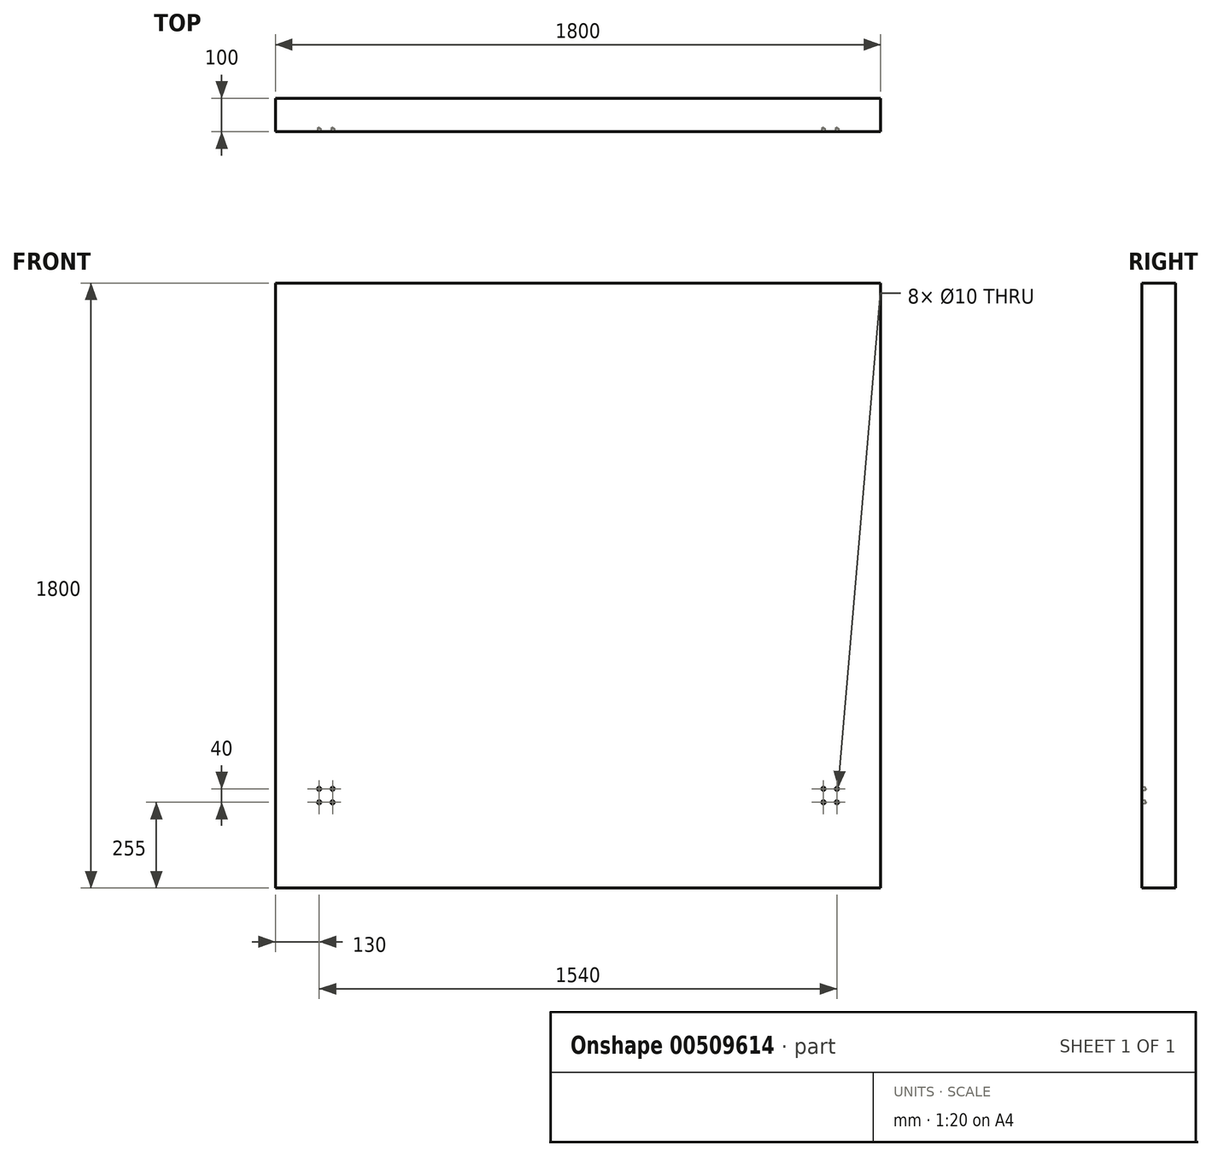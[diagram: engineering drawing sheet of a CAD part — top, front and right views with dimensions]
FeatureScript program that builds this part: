
annotation { "Feature Type Name" : "Feature", "Feature Type Description" : "" }
export const myFeature = defineFeature(function(context is Context, id is Id, definition is map)
    precondition{}
    {
        {
            var Q0;
            Q0=qCreatedBy(makeId("Front.planeOp"),FACE);
            var sketch = newSketch(context, id + "F0", { "sketchPlane" : qUnion([Q0])});
            skLineSegment(sketch, "E0.bottom", {"start": v(-900, 900) * mm, "end": v(900, 900) * mm});
            skLineSegment(sketch, "E0.top", {"start": v(-900, -900) * mm, "end": v(900, -900) * mm});
            skLineSegment(sketch, "E0.left", {"start": v(-900, 900) * mm, "end": v(-900, -900) * mm});
            skLineSegment(sketch, "E0.right", {"start": v(900, 900) * mm, "end": v(900, -900) * mm});
            skPoint(sketch, "E0.middle", {"position": v(0, 0) * mm});
            skLineSegment(sketch, "E1", {"start": v(0, 398.71) * mm, "end": v(0, -377.7) * mm, "construction": true});
            skSolve(sketch);
        }
        {
            var Q0;
            Q0=makeQuery(id+"F0.imprint","IMPRINT",FACE,{"disambiguationData":[TD([[makeQuery(id+"F0.imprint","IMPRINT",EDGE,{"derivedFrom":sQuery(id+"F0.wireOp",EDGE,"E0.bottom")}),-1.0]])]});
            extrude(context, id + "F1", {"entities" : qUnion([Q0]), "endBound" : BoundingType.SYMMETRIC, "depth" : 100 * mm});
        }
        {
            var Q0;
            Q0=makeQuery(id+"F1.opExtrude","CAP_FACE",FACE,{"disambiguationData":[OSD([sQuery(id+"F0.wireOp",EDGE,"E0.bottom"),sQuery(id+"F0.wireOp",EDGE,"E0.top"),sQuery(id+"F0.wireOp",EDGE,"E0.left"),sQuery(id+"F0.wireOp",EDGE,"E0.right")])],"isStart":false});
            var sketch = newSketch(context, id + "F2", { "sketchPlane" : qUnion([Q0])});
            skLineSegment(sketch, "E2", {"start": v(-900, -900) * mm, "end": v(-900, -625) * mm});
            skLineSegment(sketch, "E3", {"start": v(-900, -625) * mm, "end": v(-750, -625) * mm});
            skLineSegment(sketch, "E4", {"start": v(900, -900) * mm, "end": v(900, -625) * mm});
            skLineSegment(sketch, "E5", {"start": v(900, -625) * mm, "end": v(750, -625) * mm});
            skLineSegment(sketch, "E6.bottom", {"start": v(-770, -605) * mm, "end": v(-730, -605) * mm});
            skLineSegment(sketch, "E6.top", {"start": v(-770, -645) * mm, "end": v(-730, -645) * mm});
            skLineSegment(sketch, "E6.left", {"start": v(-770, -605) * mm, "end": v(-770, -645) * mm});
            skLineSegment(sketch, "E6.right", {"start": v(-730, -605) * mm, "end": v(-730, -645) * mm});
            skPoint(sketch, "E6.middle", {"position": v(-750, -625) * mm});
            skLineSegment(sketch, "E7.bottom", {"start": v(730, -605) * mm, "end": v(770, -605) * mm});
            skLineSegment(sketch, "E7.top", {"start": v(730, -645) * mm, "end": v(770, -645) * mm});
            skLineSegment(sketch, "E7.left", {"start": v(730, -605) * mm, "end": v(730, -645) * mm});
            skLineSegment(sketch, "E7.right", {"start": v(770, -605) * mm, "end": v(770, -645) * mm});
            skPoint(sketch, "E7.middle", {"position": v(750, -625) * mm});
            skSolve(sketch);
        }
        {
            var Q0;
            Q0=sQuery(id+"F2.wireOp",VERTEX,"E6.left.start");
            var Q1;
            Q1=sQuery(id+"F2.wireOp",VERTEX,"E6.right.start");
            var Q2;
            Q2=sQuery(id+"F2.wireOp",VERTEX,"E6.right.end");
            var Q3;
            Q3=sQuery(id+"F2.wireOp",VERTEX,"E6.left.end");
            var Q4;
            Q4=sQuery(id+"F2.wireOp",VERTEX,"E7.bottom.start");
            var Q5;
            Q5=sQuery(id+"F2.wireOp",VERTEX,"E7.bottom.end");
            var Q6;
            Q6=sQuery(id+"F2.wireOp",VERTEX,"E7.top.end");
            var Q7;
            Q7=sQuery(id+"F2.wireOp",VERTEX,"E7.top.start");
            var Q8;
            Q8=makeQuery(id+"F1.opExtrude","SWEPT_BODY",BODY,{"disambiguationData":[OSD([sQuery(id+"F0.wireOp",EDGE,"E0.bottom"),sQuery(id+"F0.wireOp",EDGE,"E0.top"),sQuery(id+"F0.wireOp",EDGE,"E0.left"),sQuery(id+"F0.wireOp",EDGE,"E0.right")])]});
            hole(context, id + "F3", {"style" : HoleStyle.SIMPLE, "endStyle" : HoleEndStyle.BLIND, "holeDiameter" : 10 * mm, "holeDepth" : 10 * mm, "isTappedThrough" : true, "tappedDepth" : 12 * mm, "tapClearance" : 3, "locations" : qUnion([Q0, Q1, Q2, Q3, Q4, Q5, Q6, Q7]), "scope" : qUnion([Q8])});
        }
    });
